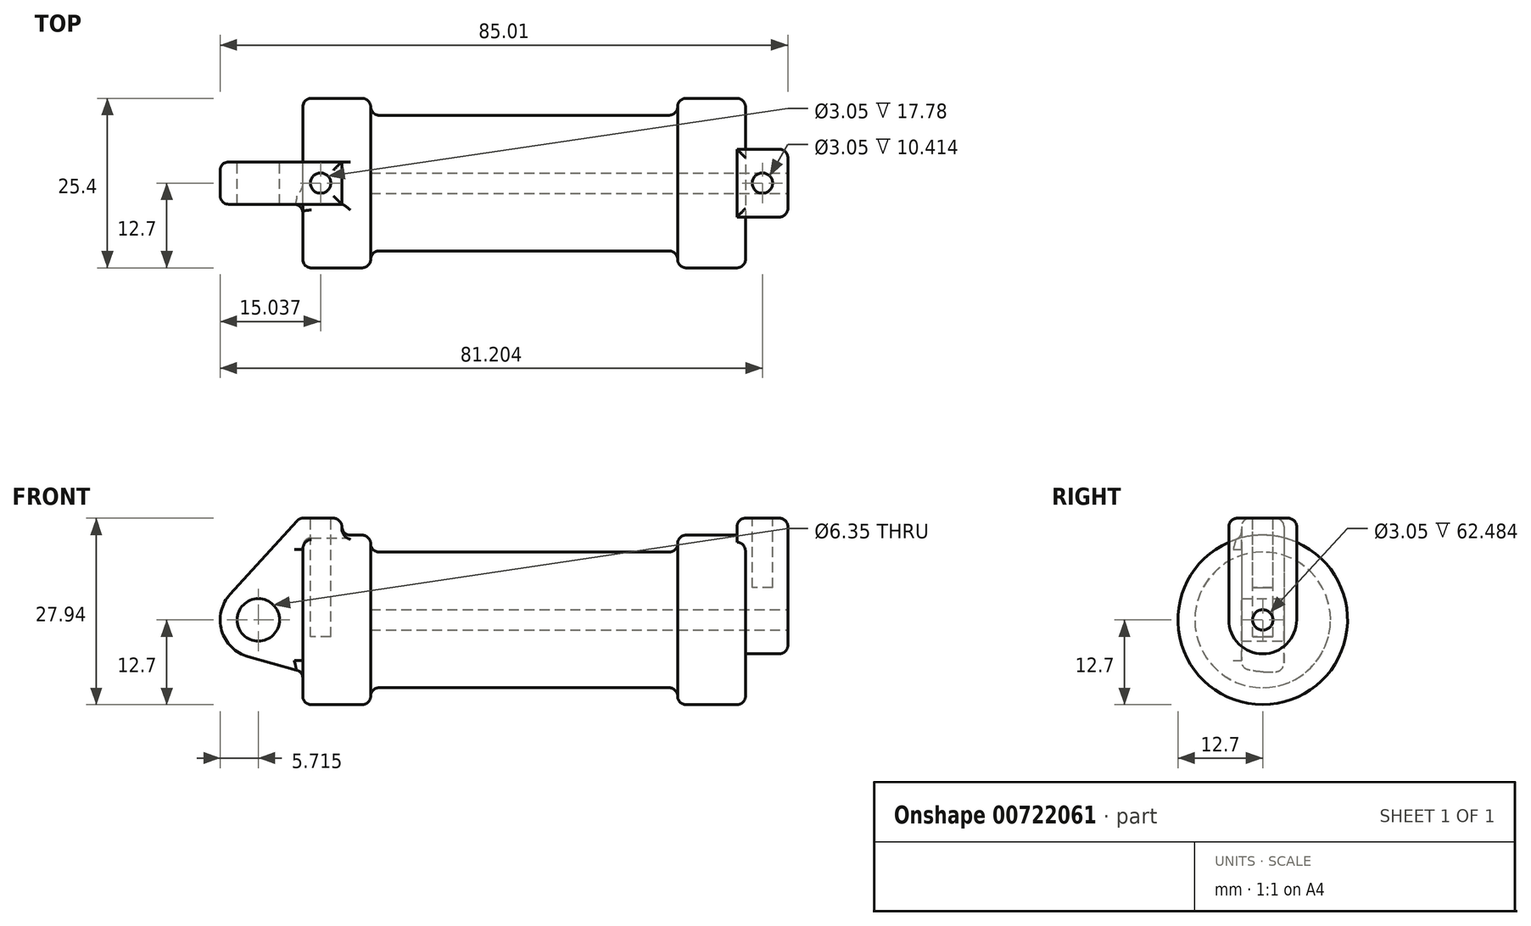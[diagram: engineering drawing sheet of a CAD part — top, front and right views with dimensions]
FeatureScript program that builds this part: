
annotation { "Feature Type Name" : "Feature", "Feature Type Description" : "" }
export const myFeature = defineFeature(function(context is Context, id is Id, definition is map)
    precondition{}
    {
        {
            var Q0;
            Q0=qCreatedBy(makeId("Front.planeOp"),FACE);
            var sketch = newSketch(context, id + "F0", { "sketchPlane" : qUnion([Q0])});
            skLineSegment(sketch, "E0", {"start": v(0, 0) * mm, "end": v(0, 12.7) * mm});
            skLineSegment(sketch, "E1", {"start": v(0, 12.7) * mm, "end": v(10.16, 12.7) * mm});
            skLineSegment(sketch, "E2", {"start": v(10.16, 12.7) * mm, "end": v(10.16, 10.16) * mm});
            skLineSegment(sketch, "E3", {"start": v(10.16, 10.16) * mm, "end": v(56.13, 10.16) * mm});
            skLineSegment(sketch, "E4", {"start": v(56.13, 10.16) * mm, "end": v(56.13, 12.7) * mm});
            skLineSegment(sketch, "E5", {"start": v(56.13, 12.7) * mm, "end": v(66.3, 12.7) * mm});
            skLineSegment(sketch, "E6", {"start": v(66.3, 12.7) * mm, "end": v(66.3, 0) * mm});
            skLineSegment(sketch, "E7", {"start": v(66.3, 0) * mm, "end": v(0, 0) * mm});
            skLineSegment(sketch, "E8", {"start": v(5.84, 15.24) * mm, "end": v(-0.5, 15.24) * mm});
            skLineSegment(sketch, "E9", {"start": v(-0.5, 15.24) * mm, "end": v(-10.88, 3.85) * mm});
            skLineSegment(sketch, "E10", {"start": v(0, 0) * mm, "end": v(-6.65, 0) * mm});
            skCircle(sketch, "E11", {"center": v(-6.65, 0) * mm, "radius": 5.72 * mm});
            skCircle(sketch, "E12", {"center": v(-6.65, 0) * mm, "radius": 3.18 * mm});
            skLineSegment(sketch, "E13", {"start": v(5.84, 15.24) * mm, "end": v(5.84, -9.4) * mm});
            skLineSegment(sketch, "E14", {"start": v(5.84, -9.4) * mm, "end": v(-8.18, -5.5) * mm});
            skLineSegment(sketch, "E15", {"start": v(10.16, 10.16) * mm, "end": v(10.16, 0) * mm});
            skSolve(sketch);
        }
        {
            var Q0;
            {var subQ0=sQuery(id+"F0.wireOp",EDGE,"E0");Q0=makeQuery(id+"F0.imprint","IMPRINT",FACE,{"disambiguationData":[TD([[makeQuery(id+"F0.imprint","IMPRINT",EDGE,{"derivedFrom":subQ0}),-1.0]])]});}
            var Q1;
            {var subQ0=sQuery(id+"F0.wireOp",EDGE,"E2");Q1=makeQuery(id+"F0.imprint","IMPRINT",FACE,{"disambiguationData":[TD([[makeQuery(id+"F0.imprint","IMPRINT",EDGE,{"derivedFrom":subQ0}),-1.0]])]});}
            var Q2;
            Q2=makeQuery(id+"F0.imprint","IMPRINT",FACE,{"disambiguationData":[TD([[makeQuery(id+"F0.imprint","IMPRINT",EDGE,{"derivedFrom":sQuery(id+"F0.wireOp",EDGE,"E3")}),-1.0]])]});
            var Q3;
            Q3=sQuery(id+"F0.wireOp",EDGE,"E7");
            revolve(context, id + "F1", {"surfaceOperationType" : NewSurfaceOperationType.NEW, "entities" : qUnion([Q0, Q1, Q2]), "axis" : qUnion([Q3]), "revolveType" : RevolveType.FULL});
        }
        {
            var Q0;
            Q0=makeQuery(id+"F1.opRevolve","SWEPT_FACE",FACE,{"disambiguationData":[OSD([sQuery(id+"F0.wireOp",EDGE,"E6")])]});
            var sketch = newSketch(context, id + "F2", { "sketchPlane" : qUnion([Q0])});
            skCircle(sketch, "E16", {"center": v(0, 0) * mm, "radius": 1.52 * mm});
            skCircle(sketch, "E17", {"center": v(0, 0) * mm, "radius": 5.08 * mm});
            skLineSegment(sketch, "E18", {"start": v(5.08, 0) * mm, "end": v(5.08, 15.24) * mm});
            skLineSegment(sketch, "E19", {"start": v(-5.08, 0) * mm, "end": v(-5.08, 15.24) * mm});
            skLineSegment(sketch, "E20", {"start": v(-5.08, 15.24) * mm, "end": v(5.08, 15.24) * mm});
            skSolve(sketch);
        }
        {
            var Q0;
            {var subQ0=sQuery(id+"F2.wireOp",EDGE,"E20");Q0=makeQuery(id+"F2.imprint","IMPRINT",FACE,{"disambiguationData":[TD([[makeQuery(id+"F2.imprint","IMPRINT",EDGE,{"derivedFrom":subQ0}),-1.0]])]});}
            extrude(context, id + "F3", {"entities" : qUnion([Q0]), "operationType" : NewBodyOperationType.ADD, "oppositeDirection" : true, "depth" : 1.27 * mm, "offsetDistance" : 25.4 * mm});
        }
        {
            var Q0;
            {var subQ0=sQuery(id+"F0.wireOp",EDGE,"E0");Q0=makeQuery(id+"F0.imprint","IMPRINT",FACE,{"disambiguationData":[TD([[makeQuery(id+"F0.imprint","IMPRINT",EDGE,{"derivedFrom":subQ0}),-1.0]])]});}
            var Q1;
            {var subQ1=sQuery(id+"F0.wireOp",EDGE,"E0");Q1=makeQuery(id+"F0.imprint","IMPRINT",FACE,{"disambiguationData":[TD([[makeQuery(id+"F0.imprint","IMPRINT",EDGE,{"derivedFrom":subQ1}),1.0]])]});}
            var Q2;
            {var subQ5=sQuery(id+"F0.wireOp",EDGE,"E12");Q2=makeQuery(id+"F0.imprint","IMPRINT",FACE,{"disambiguationData":[TD([[makeQuery(id+"F0.imprint","IMPRINT",EDGE,{"derivedFrom":subQ5}),-1.0]])]});}
            var Q3;
            {var subQ0=sQuery(id+"F0.wireOp",EDGE,"E14");Q3=makeQuery(id+"F0.imprint","IMPRINT",FACE,{"disambiguationData":[TD([[makeQuery(id+"F0.imprint","IMPRINT",EDGE,{"derivedFrom":subQ0}),-1.0]])]});}
            extrude(context, id + "F4", {"entities" : qUnion([Q0, Q1, Q2, Q3]), "operationType" : NewBodyOperationType.ADD, "depth" : 6.35 * mm, "offsetDistance" : 25.4 * mm, "symmetric" : true});
        }
        {
            var Q0;
            Q0=makeQuery(id+"F4.opExtrude","SWEPT_FACE",FACE,{"disambiguationData":[OSD([sQuery(id+"F0.wireOp",EDGE,"E8")])]});
            var sketch = newSketch(context, id + "F5", { "sketchPlane" : qUnion([Q0])});
            skCircle(sketch, "E21", {"center": v(2.67, 0) * mm, "radius": 1.52 * mm});
            skPoint(sketch, "E21.centerSnap0", {"position": v(5.84, 0) * mm});
            skPoint(sketch, "E21.centerSnap1", {"position": v(2.67, -3.18) * mm});
            skSolve(sketch);
        }
        {
            var Q0;
            Q0=makeQuery(id+"F5.imprint","IMPRINT",FACE,{"disambiguationData":[TD([[makeQuery(id+"F5.imprint","IMPRINT",EDGE,{"derivedFrom":sQuery(id+"F5.wireOp",EDGE,"E21")}),1.0]])]});
            extrude(context, id + "F6", {"entities" : qUnion([Q0]), "operationType" : NewBodyOperationType.REMOVE, "oppositeDirection" : true, "depth" : 17.78 * mm, "offsetDistance" : 25.4 * mm});
        }
        {
            var Q0;
            Q0=makeQuery(id+"F2.imprint","IMPRINT",FACE,{"disambiguationData":[TD([[makeQuery(id+"F2.imprint","IMPRINT",EDGE,{"derivedFrom":sQuery(id+"F2.wireOp",EDGE,"E16")}),1.0]])]});
            var Q1;
            Q1=sQuery(id+"F2.wireOp",EDGE,"E16");
            var Q2;
            Q2=makeQuery(id+"F1.opRevolve","SWEPT_FACE",FACE,{"disambiguationData":[OSD([sQuery(id+"F0.wireOp",EDGE,"E2")])]});
            var Q3;
            Q3=sQuery(id+"F0.wireOp",VERTEX,"E15.end");
            extrude(context, id + "F7", {"entities" : qUnion([Q0]), "operationType" : NewBodyOperationType.REMOVE, "surfaceEntities" : qUnion([Q1]), "endBound" : BoundingType.UP_TO_VERTEX, "oppositeDirection" : true, "depth" : 25.4 * mm, "endBoundEntityFace" : qUnion([Q2]), "endBoundEntityVertex" : qUnion([Q3]), "offsetDistance" : 25.4 * mm});
        }
        {
            var Q0;
            {var subQ0=sQuery(id+"F2.wireOp",EDGE,"E20");Q0=makeQuery(id+"F2.imprint","IMPRINT",FACE,{"disambiguationData":[TD([[makeQuery(id+"F2.imprint","IMPRINT",EDGE,{"derivedFrom":subQ0}),-1.0]])]});}
            var Q1;
            {var subQ0=sQuery(id+"F2.wireOp",EDGE,"E18");var subQ1=sQuery(id+"F2.wireOp",EDGE,"E17");var subQ2=makeQuery(id+"F2.imprint","INTERSECT",VERTEX,{"derivedFrom":[subQ1,subQ0]});Q1=makeQuery(id+"F2.imprint","IMPRINT",FACE,{"disambiguationData":[TD([[makeQuery(id+"F2.imprint","IMPRINT",EDGE,{"disambiguationData":[TD([[subQ2,-1.0]])],"derivedFrom":subQ1}),-1.0]])]});}
            var Q2;
            Q2=makeQuery(id+"F2.imprint","IMPRINT",FACE,{"disambiguationData":[TD([[makeQuery(id+"F2.imprint","IMPRINT",EDGE,{"derivedFrom":sQuery(id+"F2.wireOp",EDGE,"E16")}),-1.0]])]});
            extrude(context, id + "F8", {"entities" : qUnion([Q0, Q1, Q2]), "operationType" : NewBodyOperationType.ADD, "depth" : 6.35 * mm, "offsetDistance" : 25.4 * mm});
        }
        {
            var Q0;
            {var subQ0=sQuery(id+"F2.wireOp",EDGE,"E20");Q0=makeQuery(id+"F8.boolean.opBoolean","MERGE",FACE,{"derivedFrom":[makeQuery(id+"F3.opExtrude","SWEPT_FACE",FACE,{"disambiguationData":[OSD([subQ0])]}),makeQuery(id+"F8.opExtrude","SWEPT_FACE",FACE,{"disambiguationData":[OSD([subQ0])]})]});}
            var sketch = newSketch(context, id + "F9", { "sketchPlane" : qUnion([Q0])});
            skCircle(sketch, "E22", {"center": v(68.83, 0) * mm, "radius": 1.52 * mm});
            skPoint(sketch, "E22.centerSnap0", {"position": v(72.64, 0) * mm});
            skPoint(sketch, "E22.centerSnap1", {"position": v(68.83, 5.08) * mm});
            skSolve(sketch);
        }
        {
            var Q0;
            Q0=makeQuery(id+"F9.imprint","IMPRINT",FACE,{"disambiguationData":[TD([[makeQuery(id+"F9.imprint","IMPRINT",EDGE,{"derivedFrom":sQuery(id+"F9.wireOp",EDGE,"E22")}),1.0]])]});
            extrude(context, id + "F10", {"entities" : qUnion([Q0]), "operationType" : NewBodyOperationType.REMOVE, "oppositeDirection" : true, "depth" : 10.4 * mm, "offsetDistance" : 25.4 * mm});
        }
        {
            var Q0;
            {var subQ0=sQuery(id+"F2.wireOp",EDGE,"E20");var subQ1=sQuery(id+"F2.wireOp",EDGE,"E19");Q0=makeQuery(id+"F8.boolean.opBoolean","MERGE",EDGE,{"derivedFrom":[makeQuery(id+"F3.opExtrude","SWEPT_EDGE",EDGE,{"disambiguationData":[OSD([subQ1,subQ0])]}),makeQuery(id+"F8.opExtrude","SWEPT_EDGE",EDGE,{"disambiguationData":[OSD([subQ1,subQ0])]})]});}
            var Q1;
            Q1=makeQuery(id+"F8.opExtrude","CAP_EDGE",EDGE,{"disambiguationData":[OSD([sQuery(id+"F2.wireOp",EDGE,"E19")])],"isStart":true});
            var Q2;
            Q2=makeQuery(id+"F8.opExtrude","CAP_EDGE",EDGE,{"disambiguationData":[OSD([sQuery(id+"F2.wireOp",EDGE,"E18")])],"isStart":false});
            var Q3;
            Q3=makeQuery(id+"F8.opExtrude","CAP_EDGE",EDGE,{"disambiguationData":[OSD([sQuery(id+"F2.wireOp",EDGE,"E20")])],"isStart":false});
            var Q4;
            Q4=makeQuery(id+"F3.opExtrude","CAP_EDGE",EDGE,{"disambiguationData":[OSD([sQuery(id+"F2.wireOp",EDGE,"E20")])],"isStart":false});
            var Q5;
            {var subQ0=sQuery(id+"F2.wireOp",EDGE,"E20");var subQ1=sQuery(id+"F2.wireOp",EDGE,"E18");Q5=makeQuery(id+"F8.boolean.opBoolean","MERGE",EDGE,{"derivedFrom":[makeQuery(id+"F3.opExtrude","SWEPT_EDGE",EDGE,{"disambiguationData":[OSD([subQ1,subQ0])]}),makeQuery(id+"F8.opExtrude","SWEPT_EDGE",EDGE,{"disambiguationData":[OSD([subQ1,subQ0])]})]});}
            var Q6;
            Q6=makeQuery(id+"F3.opExtrude","CAP_EDGE",EDGE,{"disambiguationData":[OSD([sQuery(id+"F0.wireOp",EDGE,"E5"),sQuery(id+"F0.wireOp",EDGE,"E6")])],"isStart":false});
            fillet(context, id + "F11", {"entities" : qUnion([Q0, Q1, Q2, Q3, Q4, Q5, Q6]), "radius" : 1.27 * mm, "tangentPropagation" : true, "allowEdgeOverflow" : false});
        }
        {
            var Q0;
            Q0=makeQuery(id+"F1.opRevolve","SWEPT_EDGE",EDGE,{"disambiguationData":[OSD([sQuery(id+"F0.wireOp",EDGE,"E1"),sQuery(id+"F0.wireOp",EDGE,"E2")])]});
            var Q1;
            Q1=makeQuery(id+"F1.opRevolve","SWEPT_EDGE",EDGE,{"disambiguationData":[OSD([sQuery(id+"F0.wireOp",EDGE,"E2"),sQuery(id+"F0.wireOp",EDGE,"E3"),sQuery(id+"F0.wireOp",EDGE,"E15")])]});
            var Q2;
            Q2=makeQuery(id+"F1.opRevolve","SWEPT_EDGE",EDGE,{"disambiguationData":[OSD([sQuery(id+"F0.wireOp",EDGE,"E5"),sQuery(id+"F0.wireOp",EDGE,"E6")])]});
            var Q3;
            Q3=makeQuery(id+"F1.opRevolve","SWEPT_EDGE",EDGE,{"disambiguationData":[OSD([sQuery(id+"F0.wireOp",EDGE,"E0"),sQuery(id+"F0.wireOp",EDGE,"E1")])]});
            var Q4;
            Q4=makeQuery(id+"F1.opRevolve","SWEPT_EDGE",EDGE,{"disambiguationData":[OSD([sQuery(id+"F0.wireOp",EDGE,"E4"),sQuery(id+"F0.wireOp",EDGE,"E5")])]});
            var Q5;
            Q5=makeQuery(id+"F1.opRevolve","SWEPT_EDGE",EDGE,{"disambiguationData":[OSD([sQuery(id+"F0.wireOp",EDGE,"E3"),sQuery(id+"F0.wireOp",EDGE,"E4")])]});
            fillet(context, id + "F12", {"entities" : qUnion([Q0, Q1, Q2, Q3, Q4, Q5]), "radius" : 1.27 * mm, "tangentPropagation" : true, "allowEdgeOverflow" : false});
        }
        {
            var Q0;
            Q0=makeQuery(id+"F4.boolean.opBoolean","INTERSECT",EDGE,{"derivedFrom":[makeQuery(id+"F1.opRevolve","SWEPT_FACE",FACE,{"disambiguationData":[OSD([sQuery(id+"F0.wireOp",EDGE,"E1")])]}),makeQuery(id+"F4.opExtrude","CAP_FACE",FACE,{"disambiguationData":[OSD([sQuery(id+"F0.wireOp",EDGE,"E8"),sQuery(id+"F0.wireOp",EDGE,"E9"),sQuery(id+"F0.wireOp",EDGE,"E11"),sQuery(id+"F0.wireOp",EDGE,"E12"),sQuery(id+"F0.wireOp",EDGE,"E13"),sQuery(id+"F0.wireOp",EDGE,"E14")])],"isStart":false})]});
            var Q1;
            Q1=makeQuery(id+"F4.opExtrude","CAP_EDGE",EDGE,{"disambiguationData":[OSD([sQuery(id+"F0.wireOp",EDGE,"E9")])],"isStart":false});
            var Q2;
            Q2=makeQuery(id+"F4.opExtrude","CAP_EDGE",EDGE,{"disambiguationData":[OSD([sQuery(id+"F0.wireOp",EDGE,"E8")])],"isStart":false});
            var Q3;
            Q3=makeQuery(id+"F4.opExtrude","SWEPT_EDGE",EDGE,{"disambiguationData":[OSD([sQuery(id+"F0.wireOp",EDGE,"E8"),sQuery(id+"F0.wireOp",EDGE,"E9")])]});
            var Q4;
            Q4=makeQuery(id+"F4.opExtrude","CAP_EDGE",EDGE,{"disambiguationData":[OSD([sQuery(id+"F0.wireOp",EDGE,"E8")])],"isStart":true});
            var Q5;
            Q5=makeQuery(id+"F4.opExtrude","SWEPT_EDGE",EDGE,{"disambiguationData":[OSD([sQuery(id+"F0.wireOp",EDGE,"E8"),sQuery(id+"F0.wireOp",EDGE,"E13")])]});
            var Q6;
            Q6=makeQuery(id+"F4.boolean.opBoolean","INTERSECT",EDGE,{"derivedFrom":[makeQuery(id+"F1.opRevolve","SWEPT_FACE",FACE,{"disambiguationData":[OSD([sQuery(id+"F0.wireOp",EDGE,"E1")])]}),makeQuery(id+"F4.opExtrude","SWEPT_FACE",FACE,{"disambiguationData":[OSD([sQuery(id+"F0.wireOp",EDGE,"E13")])]})]});
            var Q7;
            Q7=makeQuery(id+"F4.opExtrude","CAP_EDGE",EDGE,{"disambiguationData":[OSD([sQuery(id+"F0.wireOp",EDGE,"E9")])],"isStart":true});
            fillet(context, id + "F13", {"entities" : qUnion([Q0, Q1, Q2, Q3, Q4, Q5, Q6, Q7]), "radius" : 1.27 * mm, "tangentPropagation" : true, "allowEdgeOverflow" : false});
        }
    });
